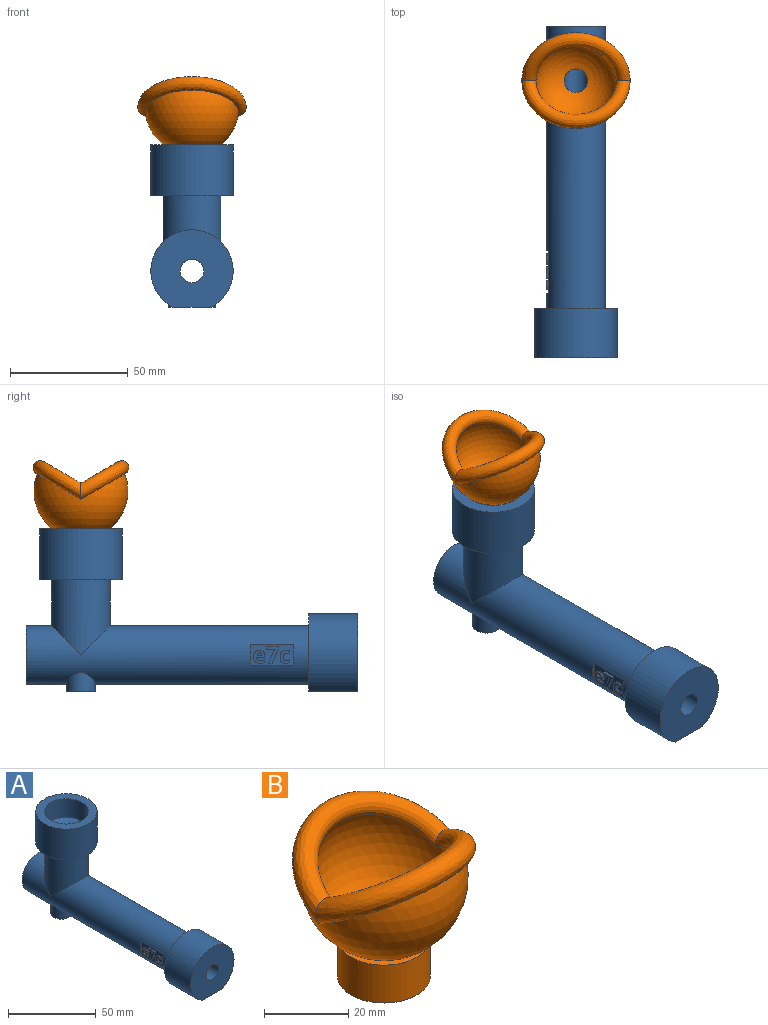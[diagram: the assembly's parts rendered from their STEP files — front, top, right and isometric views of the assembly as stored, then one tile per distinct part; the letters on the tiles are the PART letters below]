
ASSEMBLY  parts=2 mates=1
PART A: 76 faces, bbox 35x141x69 mm
  f0: cylinder r=5mm len=138mm, axis (0,-1,0), area 4240.2mm2, adj f10,f16,f73,f74,f75
  f1: plane 4x3.63mm, normal (0,1,0), area 8.3mm2, adj f5,f66,f69,f72
  f2: plane 4x3.63mm, normal (0,-1,0), area 8.3mm2, adj f5,f66,f69,f72
  f3: plane 4x3.63mm, normal (0,-1,0), area 8.3mm2, adj f5,f67,f68,f71
  f4: plane 18x9.15mm, normal (-1,0,0), area 119.1mm2, adj f5,f18,f19,f24,f25,f26,f27,f28
  f5: cylinder r=12.5mm len=120mm, axis (0,-1,0), area 8397mm2, adj f1,f2,f3,f4,f11,f14,f17,f18
  f6: cylinder r=12.5mm len=25mm, axis (0,0,-1), area 1021mm2, adj f8,f13
  f7: cylinder r=17.5mm len=35mm, axis (0,0,-1), area 2364mm2, adj f8,f12
  f8: plane 35x35mm, normal (0,0,1), area 471.2mm2, adj f6,f7
  f9: plane 11x11mm, normal (0,0,1), area 16.5mm2, adj f10,f13
  f10: cylinder r=5mm len=36mm, axis (0,0,1), area 1074.3mm2, adj f0,f9,f74,f75
  f11: cylinder r=12.5mm len=32mm, axis (0,0,-1), area 1890.7mm2, adj f5,f12
  f12: plane 35x35mm, normal (0,0,-1), area 471.2mm2, adj f7,f11
  f13: cone r=5.5mm half-angle=66.8deg, axis (0,0,1), area 430.7mm2, adj f6,f9
  f14: plane 25x25mm, normal (0,1,0), area 289.8mm2, adj f5,f73
  f15: cylinder r=17.5mm len=35mm, axis (0,1,0), area 1951.8mm2, adj f16,f17,f70
  f16: plane 35x32.97mm, normal (0,-1,0), area 861.2mm2, adj f0,f15,f70
  f17: plane 35x32.97mm, normal (0,1,0), area 448.9mm2, adj f5,f15,f70
  f18: plane 9.15x0.87mm, normal (0,-1,0), area 5.3mm2, adj f4,f5
  f19: plane 9.15x0.87mm, normal (0,1,0), area 5.3mm2, adj f4,f5
  f20: extruded ~1x0.73mm, area 0.8mm2, adj f21,f39,f40,f41
  f21: extruded ~1x0.82mm, area 0.9mm2, adj f20,f22,f40,f41
  f22: plane 2.02x1mm, normal (0,0,1), area 2mm2, adj f21,f23,f40,f41
  f23: extruded ~1x0.82mm, area 0.9mm2, adj f22,f39,f40,f41
  f24: extruded ~1.05x1mm, area 1.1mm2, adj f4,f25,f38,f40
  f25: extruded ~1x0.81mm, area 0.9mm2, adj f4,f24,f26,f40
  f26: plane 1.12x1mm, normal (0,-1,0), area 1.1mm2, adj f4,f25,f27,f40
  f27: extruded ~1x0.89mm, area 0.9mm2, adj f4,f26,f28,f40
  f28: extruded ~1x0.9mm, area 0.9mm2, adj f4,f27,f29,f40
  f29: extruded ~1x0.95mm, area 1mm2, adj f4,f28,f30,f40
  f30: extruded ~1x0.96mm, area 1.1mm2, adj f4,f29,f31,f40
  f31: plane 3.41x1mm, normal (0,0,-1), area 3.4mm2, adj f4,f30,f32,f40
  f32: plane 1x0.7mm, normal (0,-1,0), area 0.7mm2, adj f4,f31,f33,f40
  f33: extruded ~1.76x1mm, area 1.9mm2, adj f4,f32,f34,f40
  f34: extruded ~1.74x1mm, area 1.9mm2, adj f4,f33,f35,f40
  f35: extruded ~1.84x1mm, area 2mm2, adj f4,f34,f36,f40
  f36: extruded ~2.05x1mm, area 2.2mm2, adj f4,f35,f37,f40
  f37: extruded ~2x1mm, area 2.2mm2, adj f4,f36,f38,f40
  f38: extruded ~1.99x1mm, area 2.2mm2, adj f4,f24,f37,f40
  f39: extruded ~1x0.72mm, area 0.8mm2, adj f20,f23,f40,f41
  f40: plane 5.48x4.87mm, normal (-1,0,0), area 16.9mm2, adj f20,f21,f22,f23,f24,f25,f26,f27
  f41: plane 2.02x1.12mm, normal (-1,0,0), area 1.8mm2, adj f20,f21,f22,f23,f39
  f42: plane 1.53x1mm, normal (0,0,-1), area 1.5mm2, adj f4,f43,f48,f49
  f43: plane 6x2.61mm, normal (0,-0.92,-0.4), area 6.5mm2, adj f4,f42,f44,f49
  f44: plane 1x0.92mm, normal (0,-1,0), area 0.9mm2, adj f4,f43,f45,f49
  f45: plane 4.96x1mm, normal (0,0,1), area 5mm2, adj f4,f44,f46,f49
  f46: plane 1.23x1mm, normal (0,1,0), area 1.2mm2, adj f4,f45,f47,f49
  f47: plane 3.41x1mm, normal (0,0,-1), area 3.4mm2, adj f4,f46,f48,f49
  f48: plane 5.68x2.6mm, normal (0,0.91,0.42), area 6.2mm2, adj f4,f42,f47,f49
  f49: plane 6.91x4.96mm, normal (-1,0,0), area 14.5mm2, adj f42,f43,f44,f45,f46,f47,f48
  f50: extruded ~1x0.9mm, area 0.9mm2, adj f4,f51,f63,f64
  f51: extruded ~1x0.71mm, area 0.8mm2, adj f4,f50,f52,f64
  f52: plane 1.23x1mm, normal (0,-1,0), area 1.2mm2, adj f4,f51,f53,f64
  f53: extruded ~1x0.71mm, area 0.8mm2, adj f4,f52,f54,f64
  f54: extruded ~1x0.77mm, area 0.8mm2, adj f4,f53,f55,f64
  f55: extruded ~1.55x1.13mm, area 2.2mm2, adj f4,f54,f56,f64
  f56: extruded ~1.6x1.13mm, area 2.2mm2, adj f4,f55,f57,f64
  f57: extruded ~1x0.59mm, area 0.6mm2, adj f4,f56,f58,f64
  f58: extruded ~1x0.63mm, area 0.7mm2, adj f4,f57,f59,f64
  f59: plane 1.12x1mm, normal (0,-0.93,-0.36), area 1.2mm2, adj f4,f58,f60,f64
  f60: extruded ~1.65x1mm, area 1.7mm2, adj f4,f59,f61,f64
  f61: extruded ~1.92x1mm, area 2.1mm2, adj f4,f60,f62,f64
  f62: extruded ~2.06x1mm, area 2.2mm2, adj f4,f61,f63,f64
  f63: extruded ~2.71x2.47mm, area 4.2mm2, adj f4,f50,f62,f64
  f64: plane 5.48x4.24mm, normal (-1,0,0), area 12.4mm2, adj f50,f51,f52,f53,f54,f55,f56,f57
  f65: plane 4x3.63mm, normal (0,1,0), area 8.3mm2, adj f5,f67,f68,f71
  f66: plane 12x2.98mm, normal (0.71,0,-0.71), area 50.5mm2, adj f1,f2,f67,f69
  f67: plane 12x2.98mm, normal (-0.71,0,-0.71), area 50.5mm2, adj f3,f65,f66,f68
  f68: plane 12x7.02mm, normal (0,0,-1), area 68.8mm2, adj f3,f65,f67,f71
  f69: plane 12x7.02mm, normal (0,0,-1), area 68.8mm2, adj f1,f2,f66,f72
  f70: plane 21x16.35mm, normal (0,0,-1), area 343.4mm2, adj f15,f16,f17
  f71: cylinder r=6mm len=12mm, axis (0,0,-1), area 113.2mm2, adj f3,f5,f65,f68
  f72: cylinder r=6mm len=12mm, axis (0,0,-1), area 113.2mm2, adj f1,f2,f5,f69
  f73: torus R=8mm, axis (0,-1,0), area 180.3mm2, adj f0,f14
  f74: plane 3.06x0.24mm, normal (0,0,1), area 0.5mm2, adj f0,f10
  f75: plane 3.06x0.24mm, normal (0,0,1), area 0.5mm2, adj f0,f10
PART B: 8 faces, bbox 46x40.6x42 mm
  f0: cylinder r=5mm len=12.75mm, axis (0,0,-1), area 400.6mm2, adj f3,f5
  f1: cylinder r=11mm len=22mm, axis (0,0,-1), area 760.3mm2, adj f2,f3
  f2: plane 22x22mm, normal (0,0,1), area 141.4mm2, adj f1,f4
  f3: plane 22x22mm, normal (0,0,-1), area 301.6mm2, adj f0,f1
  f4: sphere r=20mm, area 2713.5mm2, adj f2,f6,f7
  f5: sphere r=17mm, area 2333.5mm2, adj f0,f6,f7
  f6: bspline ~45.95x23.27mm, area 940mm2, adj f4,f5,f7
  f7: bspline ~45.95x23.28mm, area 921.4mm2, adj f4,f5,f6
PLACE A at identity
PLACE B t=(0,36.69,3)mm
MATE fastened B.f0 <-> A.f6  axis (0,0,-1) through (0,36.69,3)mm
